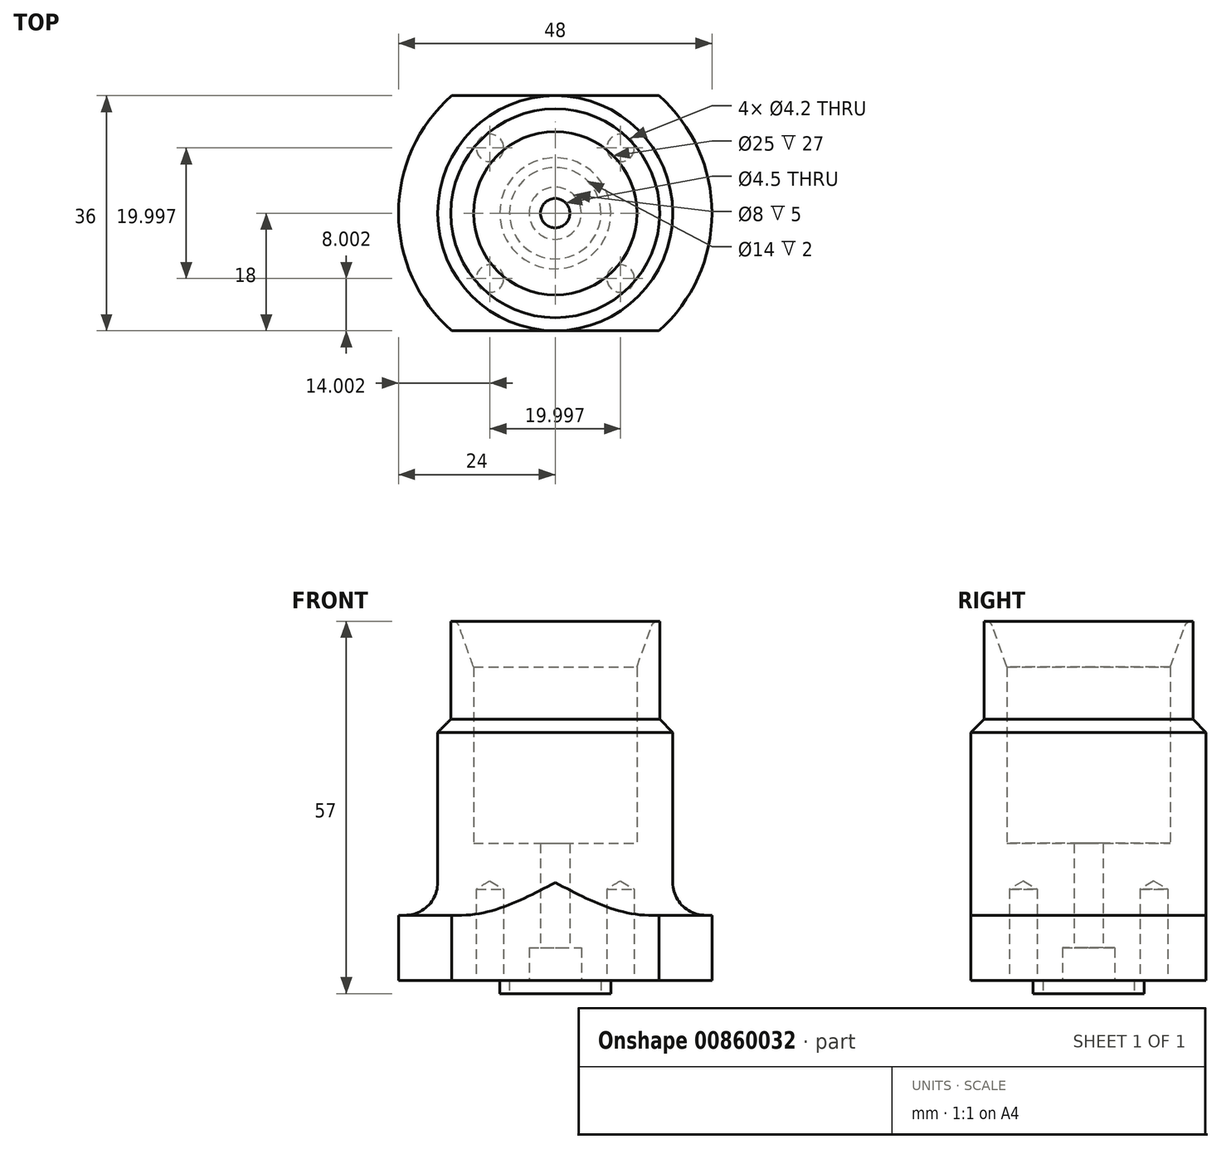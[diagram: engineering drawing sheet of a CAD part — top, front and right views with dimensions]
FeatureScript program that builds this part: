
annotation { "Feature Type Name" : "Feature", "Feature Type Description" : "" }
export const myFeature = defineFeature(function(context is Context, id is Id, definition is map)
    precondition{}
    {
        {
            var Q0;
            Q0=qCreatedBy(makeId("Front.planeOp"),FACE);
            var sketch = newSketch(context, id + "F0", { "sketchPlane" : qUnion([Q0])});
            skLineSegment(sketch, "E0", {"start": v(4, 2) * mm, "end": v(4, 7) * mm});
            skLineSegment(sketch, "E1", {"start": v(4, 7) * mm, "end": v(2.25, 7) * mm});
            skLineSegment(sketch, "E2", {"start": v(2.25, 7) * mm, "end": v(2.25, 23) * mm});
            skLineSegment(sketch, "E3", {"start": v(2.25, 23) * mm, "end": v(12.5, 23) * mm});
            skLineSegment(sketch, "E4", {"start": v(12.5, 23) * mm, "end": v(12.5, 50) * mm});
            skLineSegment(sketch, "E5", {"start": v(12.5, 50) * mm, "end": v(14.76, 56.34) * mm});
            skLineSegment(sketch, "E6", {"start": v(15.7, 57) * mm, "end": v(16, 57) * mm});
            skLineSegment(sketch, "E7", {"start": v(16, 57) * mm, "end": v(16, 42) * mm});
            skLineSegment(sketch, "E8", {"start": v(16, 42) * mm, "end": v(18, 40) * mm});
            skLineSegment(sketch, "E9", {"start": v(24, 12) * mm, "end": v(24, 2) * mm});
            skLineSegment(sketch, "E10", {"start": v(24, 2) * mm, "end": v(8.5, 2) * mm});
            skLineSegment(sketch, "E11", {"start": v(8.5, 2) * mm, "end": v(8.5, 0) * mm});
            skLineSegment(sketch, "E12", {"start": v(8.5, 0) * mm, "end": v(7, 0) * mm});
            skLineSegment(sketch, "E13", {"start": v(4, 2) * mm, "end": v(7, 2) * mm});
            skLineSegment(sketch, "E14", {"start": v(7, 2) * mm, "end": v(7, 0) * mm});
            skLineSegment(sketch, "E15", {"start": v(18, 40) * mm, "end": v(18, 17) * mm});
            skLineSegment(sketch, "E16", {"start": v(23, 12) * mm, "end": v(24, 12) * mm});
            skPoint(sketch, "E17.visualSharp", {"position": v(18, 12) * mm});
            skArc(sketch, "E17.filletArc", {"start": v(18, 17) * mm, "mid": v(19.46, 13.46) * mm, "end": v(23, 12) * mm});
            skPoint(sketch, "E18.visualSharp", {"position": v(15, 57) * mm});
            skArc(sketch, "E18.filletArc", {"start": v(15.7, 57) * mm, "mid": v(15.13, 56.82) * mm, "end": v(14.76, 56.34) * mm});
            skLineSegment(sketch, "E19", {"start": v(0, 0) * mm, "end": v(0, 81.2) * mm, "construction": true});
            skSolve(sketch);
        }
        {
            var Q0;
            Q0=makeQuery(id+"F0.imprint","IMPRINT",FACE,{"disambiguationData":[TD([[makeQuery(id+"F0.imprint","IMPRINT",EDGE,{"derivedFrom":sQuery(id+"F0.wireOp",EDGE,"E0")}),-1.0]])]});
            var Q1;
            Q1=sQuery(id+"F0.wireOp",EDGE,"E19");
            revolve(context, id + "F1", {"surfaceOperationType" : NewSurfaceOperationType.NEW, "entities" : qUnion([Q0]), "axis" : qUnion([Q1]), "revolveType" : RevolveType.FULL});
        }
        {
            var Q0;
            Q0=qCreatedBy(makeId("Top.planeOp"),FACE);
            var sketch = newSketch(context, id + "F2", { "sketchPlane" : qUnion([Q0])});
            skLineSegment(sketch, "E20.bottom", {"start": v(32.5, 18) * mm, "end": v(-32.5, 18) * mm});
            skLineSegment(sketch, "E20.top", {"start": v(32.5, -18) * mm, "end": v(-32.5, -18) * mm});
            skLineSegment(sketch, "E20.left", {"start": v(32.5, 18) * mm, "end": v(32.5, -18) * mm});
            skLineSegment(sketch, "E20.right", {"start": v(-32.5, 18) * mm, "end": v(-32.5, -18) * mm});
            skPoint(sketch, "E20.middle", {"position": v(0, 0) * mm});
            skLineSegment(sketch, "E21.bottom", {"start": v(35, 28) * mm, "end": v(-35, 28) * mm});
            skLineSegment(sketch, "E21.top", {"start": v(35, -28) * mm, "end": v(-35, -28) * mm});
            skLineSegment(sketch, "E21.left", {"start": v(35, 28) * mm, "end": v(35, -28) * mm});
            skLineSegment(sketch, "E21.right", {"start": v(-35, 28) * mm, "end": v(-35, -28) * mm});
            skSolve(sketch);
        }
        {
            var Q0;
            Q0=makeQuery(id+"F2.imprint","IMPRINT",FACE,{"disambiguationData":[TD([[makeQuery(id+"F2.imprint","IMPRINT",EDGE,{"derivedFrom":sQuery(id+"F2.wireOp",EDGE,"E20.bottom")}),-1.0]])]});
            extrude(context, id + "F3", {"entities" : qUnion([Q0]), "operationType" : NewBodyOperationType.REMOVE, "endBound" : BoundingType.THROUGH_ALL, "depth" : 25 * mm, "offsetDistance" : 25 * mm});
        }
        {
            var Q0;
            Q0=makeQuery(id+"F1.opRevolve","SWEPT_FACE",FACE,{"disambiguationData":[OSD([sQuery(id+"F0.wireOp",EDGE,"E10")])]});
            var sketch = newSketch(context, id + "F4", { "sketchPlane" : qUnion([Q0])});
            skCircle(sketch, "E22", {"center": v(0, 0) * mm, "radius": 14.14 * mm, "construction": true});
            skPoint(sketch, "E23", {"position": v(-10, 10) * mm});
            skPoint(sketch, "E24", {"position": v(10, 10) * mm});
            skLineSegment(sketch, "E25", {"start": v(-10, 10) * mm, "end": v(0, 0) * mm, "construction": true});
            skLineSegment(sketch, "E26", {"start": v(0, 0) * mm, "end": v(10, 10) * mm, "construction": true});
            skPoint(sketch, "E27.MirrorP", {"position": v(-10, -10) * mm});
            skPoint(sketch, "E28.MirrorP", {"position": v(10, -10) * mm});
            skSolve(sketch);
        }
        {
            var Q0;
            Q0=sQuery(id+"F4.wireOp",VERTEX,"E23");
            var Q1;
            Q1=sQuery(id+"F4.wireOp",VERTEX,"E24");
            var Q2;
            Q2=sQuery(id+"F4.wireOp",VERTEX,"E28.MirrorP");
            var Q3;
            Q3=sQuery(id+"F4.wireOp",VERTEX,"E27.MirrorP");
            var Q4;
            Q4=makeQuery(id+"F1.opRevolve","SWEPT_BODY",BODY,{"disambiguationData":[OSD([sQuery(id+"F0.wireOp",EDGE,"E0"),sQuery(id+"F0.wireOp",EDGE,"E1"),sQuery(id+"F0.wireOp",EDGE,"E2"),sQuery(id+"F0.wireOp",EDGE,"E3"),sQuery(id+"F0.wireOp",EDGE,"E4"),sQuery(id+"F0.wireOp",EDGE,"E5"),sQuery(id+"F0.wireOp",EDGE,"E6"),sQuery(id+"F0.wireOp",EDGE,"E7"),sQuery(id+"F0.wireOp",EDGE,"E8"),sQuery(id+"F0.wireOp",EDGE,"E9"),sQuery(id+"F0.wireOp",EDGE,"E10"),sQuery(id+"F0.wireOp",EDGE,"E11"),sQuery(id+"F0.wireOp",EDGE,"E12"),sQuery(id+"F0.wireOp",EDGE,"E13"),sQuery(id+"F0.wireOp",EDGE,"E14"),sQuery(id+"F0.wireOp",EDGE,"E15"),sQuery(id+"F0.wireOp",EDGE,"E16"),sQuery(id+"F0.wireOp",EDGE,"E17.filletArc"),sQuery(id+"F0.wireOp",EDGE,"E18.filletArc")])]});
            hole(context, id + "F5", {"style" : HoleStyle.SIMPLE, "endStyle" : HoleEndStyle.BLIND, "standardTappedOrClearance" : lookupTablePath({ "standard" : "ISO", "engagement" : "75%", "pitch" : "0.8 mm", "size" : "M5", "type" : "Tapped" }), "standardBlindInLast" : lookupTablePath({ "standard" : "ISO", "fit" : "Normal", "engagement" : "75%", "pitch" : "0.8 mm", "size" : "M5", "type" : "Clearance & tapped" }), "holeDiameter" : 4.2 * mm, "majorDiameter" : 5 * mm, "showTappedDepth" : true, "holeDepth" : 14 * mm, "isTappedThrough" : true, "tappedDepth" : 10 * mm, "tapClearance" : 5, "locations" : qUnion([Q0, Q1, Q2, Q3]), "scope" : qUnion([Q4])});
        }
    });
